# Revit family: 3-763-xx - Verve Wall Sconce
name_source: partatom
category: Luminarias
units: mm (PartAtom-declared; Revit-internal decimal feet)

## family parameters
Anfitrión = Muro
Compartido = No
Corte con vacíos al cargar = No
Cota de conector redondo = Diámetro de uso
Número OmniClass = 23.80.70.00
Origen de luz = Sí
Punto de cálculo de habitación = No
Siempre vertical = Sí
Tipo de pieza = Normal
Título OmniClass = Lighting

## types (1)
- 3-763-15 / Black
    Archivo de red fotométrica = 3-763-15 Verve 22 Sconce.ies
    Cambio de temperatura de color de luz atenuada = <Ninguno>
    Comentarios de vataje = 1 x 18.0 W at 120 V
    Elevación por defecto = 0 mm  [stored 0 ft]
    Fabricante = Oxygen Lighting and Fans
    Filtro de color = 16777215
    Lámpara = LED Array
    Metal Finish 1 = 6 - White
    Metal Finish 2 = 15 - Black
    Modelo = 3-763-xx / Verve Wall Sconce
    References = Ref. 3 = 120 V / Ref. 37 = 277 V
    URL = www.oxygenlighting.com
    Voltage = 120 V
    Voltage Input = 120 V or 277 V - 50/60 Hz
    Ángulo de inclinación = 90.00°

note: [stored X ft] marks values corroborated as IEEE doubles in the binary element streams (Revit-internal decimal feet)

## geometry (parser evidence)
native form markers: Extrusion x1, Sweep x5
no freeform markers — native parametric forms only
